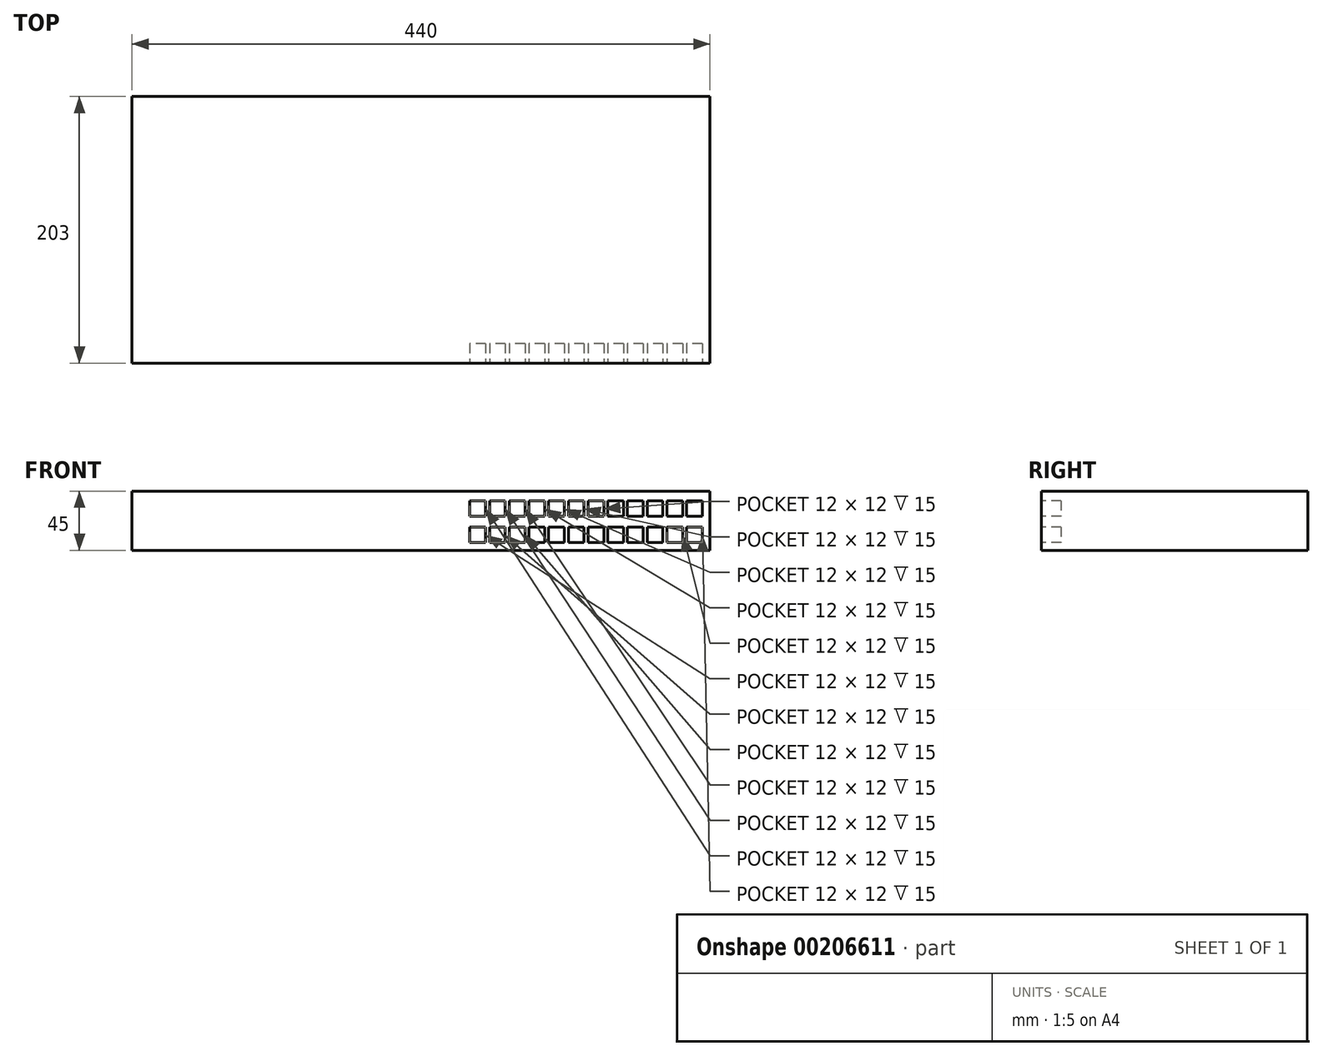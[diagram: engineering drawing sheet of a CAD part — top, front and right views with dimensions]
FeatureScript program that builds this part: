
annotation { "Feature Type Name" : "Feature", "Feature Type Description" : "" }
export const myFeature = defineFeature(function(context is Context, id is Id, definition is map)
    precondition{}
    {
        {
            var Q0;
            Q0=qCreatedBy(makeId("Front.planeOp"),FACE);
            var sketch = newSketch(context, id + "F0", { "sketchPlane" : qUnion([Q0])});
            skLineSegment(sketch, "E0.bottom", {"start": v(0, 0) * mm, "end": v(440, 0) * mm});
            skLineSegment(sketch, "E0.top", {"start": v(0, 45) * mm, "end": v(440, 45) * mm});
            skLineSegment(sketch, "E0.left", {"start": v(0, 0) * mm, "end": v(0, 45) * mm});
            skLineSegment(sketch, "E0.right", {"start": v(440, 0) * mm, "end": v(440, 45) * mm});
            skSolve(sketch);
        }
        {
            var Q0;
            Q0 = qSketchRegion(id + "F0", true);
            extrude(context, id + "F1", {"entities" : qUnion([Q0]), "depth" : 203 * mm});
        }
        {
            var Q0;
            Q0=makeQuery(id+"F1.opExtrude","CAP_FACE",FACE,{"disambiguationData":[OSD([sQuery(id+"F0.wireOp",EDGE,"E0.bottom"),sQuery(id+"F0.wireOp",EDGE,"E0.top"),sQuery(id+"F0.wireOp",EDGE,"E0.left"),sQuery(id+"F0.wireOp",EDGE,"E0.right")])],"isStart":false});
            var sketch = newSketch(context, id + "F2", { "sketchPlane" : qUnion([Q0])});
            skLineSegment(sketch, "E1", {"start": v(434.2, 37.78) * mm, "end": v(422.2, 37.78) * mm});
            skLineSegment(sketch, "E2", {"start": v(434.2, 37.78) * mm, "end": v(434.2, 25.78) * mm});
            skLineSegment(sketch, "E3.1.0.0", {"start": v(419.2, 37.78) * mm, "end": v(419.2, 25.78) * mm});
            skLineSegment(sketch, "E3.2.0.0", {"start": v(404.2, 37.78) * mm, "end": v(404.2, 25.78) * mm});
            skLineSegment(sketch, "E3.3.0.0", {"start": v(389.2, 37.78) * mm, "end": v(389.2, 25.78) * mm});
            skLineSegment(sketch, "E3.4.0.0", {"start": v(374.2, 37.78) * mm, "end": v(374.2, 25.78) * mm});
            skLineSegment(sketch, "E3.5.0.0", {"start": v(359.2, 37.78) * mm, "end": v(359.2, 25.78) * mm});
            skLineSegment(sketch, "E3.6.0.0", {"start": v(344.2, 37.78) * mm, "end": v(344.2, 25.78) * mm});
            skLineSegment(sketch, "E3.7.0.0", {"start": v(329.2, 37.78) * mm, "end": v(329.2, 25.78) * mm});
            skLineSegment(sketch, "E3.8.0.0", {"start": v(314.2, 37.78) * mm, "end": v(314.2, 25.78) * mm});
            skLineSegment(sketch, "E3.9.0.0", {"start": v(299.2, 37.78) * mm, "end": v(299.2, 25.78) * mm});
            skLineSegment(sketch, "E3.10.0.0", {"start": v(284.2, 37.78) * mm, "end": v(284.2, 25.78) * mm});
            skLineSegment(sketch, "E3.11.0.0", {"start": v(269.2, 37.78) * mm, "end": v(269.2, 25.78) * mm});
            skLineSegment(sketch, "E3.direction1", {"start": v(434.2, 5.78) * mm, "end": v(419.2, 5.78) * mm, "construction": true});
            skLineSegment(sketch, "E4.0", {"start": v(422.2, 37.78) * mm, "end": v(422.2, 25.78) * mm});
            skLineSegment(sketch, "E5.1.0.0", {"start": v(407.2, 37.78) * mm, "end": v(407.2, 25.78) * mm});
            skLineSegment(sketch, "E5.2.0.0", {"start": v(392.2, 37.78) * mm, "end": v(392.2, 25.78) * mm});
            skLineSegment(sketch, "E5.3.0.0", {"start": v(377.2, 37.78) * mm, "end": v(377.2, 25.78) * mm});
            skLineSegment(sketch, "E5.4.0.0", {"start": v(362.2, 37.78) * mm, "end": v(362.2, 25.78) * mm});
            skLineSegment(sketch, "E5.5.0.0", {"start": v(347.2, 37.78) * mm, "end": v(347.2, 25.78) * mm});
            skLineSegment(sketch, "E5.6.0.0", {"start": v(332.2, 37.78) * mm, "end": v(332.2, 25.78) * mm});
            skLineSegment(sketch, "E5.7.0.0", {"start": v(317.2, 37.78) * mm, "end": v(317.2, 25.78) * mm});
            skLineSegment(sketch, "E5.8.0.0", {"start": v(302.2, 37.78) * mm, "end": v(302.2, 25.78) * mm});
            skLineSegment(sketch, "E5.9.0.0", {"start": v(287.2, 37.78) * mm, "end": v(287.2, 25.78) * mm});
            skLineSegment(sketch, "E5.10.0.0", {"start": v(272.2, 37.78) * mm, "end": v(272.2, 25.78) * mm});
            skLineSegment(sketch, "E5.11.0.0", {"start": v(257.2, 37.78) * mm, "end": v(257.2, 25.78) * mm});
            skLineSegment(sketch, "E5.direction1", {"start": v(419.2, 5.78) * mm, "end": v(407.2, 5.78) * mm, "construction": true});
            skLineSegment(sketch, "E6", {"start": v(434.2, 25.78) * mm, "end": v(422.2, 25.78) * mm});
            skLineSegment(sketch, "E7", {"start": v(434.2, 17.78) * mm, "end": v(422.2, 17.78) * mm});
            skLineSegment(sketch, "E8", {"start": v(434.2, 5.78) * mm, "end": v(407.2, 5.78) * mm});
            skPoint(sketch, "E9.orphan", {"position": v(242.2, 38.76) * mm});
            skPoint(sketch, "E10.orphan", {"position": v(257.2, 38.76) * mm});
            skLineSegment(sketch, "E11.trimOffspring", {"start": v(269.2, 37.78) * mm, "end": v(257.2, 37.78) * mm});
            skPoint(sketch, "E12.orphan", {"position": v(272.2, 38.76) * mm});
            skLineSegment(sketch, "E13.trimOffspring", {"start": v(269.2, 25.78) * mm, "end": v(257.2, 25.78) * mm});
            skLineSegment(sketch, "E14.trimOffspring", {"start": v(269.2, 17.78) * mm, "end": v(269.2, 5.78) * mm});
            skLineSegment(sketch, "E15.trimOffspring", {"start": v(257.2, 17.78) * mm, "end": v(257.2, 5.78) * mm});
            skLineSegment(sketch, "E16.trimOffspring", {"start": v(272.2, 17.78) * mm, "end": v(272.2, 5.78) * mm});
            skLineSegment(sketch, "E17.trimOffspring", {"start": v(284.2, 17.78) * mm, "end": v(284.2, 5.78) * mm});
            skLineSegment(sketch, "E18.trimOffspring", {"start": v(287.2, 17.78) * mm, "end": v(287.2, 5.78) * mm});
            skLineSegment(sketch, "E19.trimOffspring", {"start": v(269.2, 17.78) * mm, "end": v(257.2, 17.78) * mm});
            skLineSegment(sketch, "E20.trimOffspring", {"start": v(269.2, 5.78) * mm, "end": v(257.2, 5.78) * mm});
            skLineSegment(sketch, "E21.trimOffspring", {"start": v(284.2, 17.78) * mm, "end": v(272.2, 17.78) * mm});
            skLineSegment(sketch, "E22.trimOffspring", {"start": v(299.2, 17.78) * mm, "end": v(299.2, 5.78) * mm});
            skLineSegment(sketch, "E23.trimOffspring", {"start": v(302.2, 17.78) * mm, "end": v(302.2, 5.78) * mm});
            skLineSegment(sketch, "E24.trimOffspring", {"start": v(314.2, 17.78) * mm, "end": v(314.2, 5.78) * mm});
            skLineSegment(sketch, "E25.trimOffspring", {"start": v(317.2, 17.78) * mm, "end": v(317.2, 5.78) * mm});
            skLineSegment(sketch, "E26.trimOffspring", {"start": v(314.2, 17.78) * mm, "end": v(302.2, 17.78) * mm});
            skLineSegment(sketch, "E27.trimOffspring", {"start": v(314.2, 5.78) * mm, "end": v(302.2, 5.78) * mm});
            skLineSegment(sketch, "E28.trimOffspring", {"start": v(299.2, 5.78) * mm, "end": v(272.2, 5.78) * mm});
            skLineSegment(sketch, "E29.trimOffspring", {"start": v(299.2, 17.78) * mm, "end": v(287.2, 17.78) * mm});
            skLineSegment(sketch, "E30.trimOffspring", {"start": v(299.2, 25.78) * mm, "end": v(287.2, 25.78) * mm});
            skLineSegment(sketch, "E31.trimOffspring", {"start": v(299.2, 37.78) * mm, "end": v(287.2, 37.78) * mm});
            skLineSegment(sketch, "E32.trimOffspring", {"start": v(314.2, 37.78) * mm, "end": v(302.2, 37.78) * mm});
            skLineSegment(sketch, "E33.trimOffspring", {"start": v(314.2, 25.78) * mm, "end": v(302.2, 25.78) * mm});
            skPoint(sketch, "E34.orphan", {"position": v(317.2, 38.76) * mm});
            skPoint(sketch, "E35.orphan", {"position": v(302.2, 38.76) * mm});
            skPoint(sketch, "E36.orphan", {"position": v(287.2, 38.76) * mm});
            skLineSegment(sketch, "E37.trimOffspring", {"start": v(284.2, 37.78) * mm, "end": v(272.2, 37.78) * mm});
            skLineSegment(sketch, "E38.trimOffspring", {"start": v(284.2, 25.78) * mm, "end": v(272.2, 25.78) * mm});
            skLineSegment(sketch, "E39.trimOffspring", {"start": v(329.2, 37.78) * mm, "end": v(317.2, 37.78) * mm});
            skLineSegment(sketch, "E40.trimOffspring", {"start": v(329.2, 25.78) * mm, "end": v(317.2, 25.78) * mm});
            skLineSegment(sketch, "E41.trimOffspring", {"start": v(329.2, 17.78) * mm, "end": v(317.2, 17.78) * mm});
            skLineSegment(sketch, "E42.trimOffspring", {"start": v(332.2, 17.78) * mm, "end": v(332.2, 5.78) * mm});
            skLineSegment(sketch, "E43.trimOffspring", {"start": v(329.2, 5.78) * mm, "end": v(317.2, 5.78) * mm});
            skLineSegment(sketch, "E44.trimOffspring", {"start": v(344.2, 5.78) * mm, "end": v(332.2, 5.78) * mm});
            skLineSegment(sketch, "E45.trimOffspring", {"start": v(344.2, 17.78) * mm, "end": v(332.2, 17.78) * mm});
            skLineSegment(sketch, "E46.trimOffspring", {"start": v(344.2, 25.78) * mm, "end": v(332.2, 25.78) * mm});
            skLineSegment(sketch, "E47.trimOffspring", {"start": v(329.2, 17.78) * mm, "end": v(329.2, 5.78) * mm});
            skLineSegment(sketch, "E48.trimOffspring", {"start": v(344.2, 17.78) * mm, "end": v(344.2, 5.78) * mm});
            skLineSegment(sketch, "E49.trimOffspring", {"start": v(347.2, 17.78) * mm, "end": v(347.2, 5.78) * mm});
            skLineSegment(sketch, "E50.trimOffspring", {"start": v(359.2, 17.78) * mm, "end": v(359.2, 5.78) * mm});
            skLineSegment(sketch, "E51.trimOffspring", {"start": v(362.2, 17.78) * mm, "end": v(362.2, 5.78) * mm});
            skLineSegment(sketch, "E52.trimOffspring", {"start": v(374.2, 17.78) * mm, "end": v(374.2, 5.78) * mm});
            skLineSegment(sketch, "E53.trimOffspring", {"start": v(377.2, 17.78) * mm, "end": v(377.2, 5.78) * mm});
            skLineSegment(sketch, "E54.trimOffspring", {"start": v(389.2, 17.78) * mm, "end": v(389.2, 5.78) * mm});
            skLineSegment(sketch, "E55.trimOffspring", {"start": v(407.2, 17.78) * mm, "end": v(407.2, 5.78) * mm});
            skLineSegment(sketch, "E56.trimOffspring", {"start": v(419.2, 17.78) * mm, "end": v(419.2, 5.78) * mm});
            skLineSegment(sketch, "E57.trimOffspring", {"start": v(422.2, 17.78) * mm, "end": v(422.2, 5.78) * mm});
            skLineSegment(sketch, "E58.trimOffspring", {"start": v(434.2, 17.78) * mm, "end": v(434.2, 5.78) * mm});
            skLineSegment(sketch, "E59.trimOffspring", {"start": v(419.2, 17.78) * mm, "end": v(407.2, 17.78) * mm});
            skLineSegment(sketch, "E60.trimOffspring", {"start": v(404.2, 17.78) * mm, "end": v(392.2, 17.78) * mm});
            skLineSegment(sketch, "E61.trimOffspring", {"start": v(404.2, 17.78) * mm, "end": v(404.2, 5.78) * mm});
            skLineSegment(sketch, "E62.trimOffspring", {"start": v(392.2, 17.78) * mm, "end": v(392.2, 5.78) * mm});
            skLineSegment(sketch, "E63.trimOffspring", {"start": v(389.2, 17.78) * mm, "end": v(377.2, 17.78) * mm});
            skLineSegment(sketch, "E64.trimOffspring", {"start": v(389.2, 5.78) * mm, "end": v(362.2, 5.78) * mm});
            skLineSegment(sketch, "E65.trimOffspring", {"start": v(404.2, 5.78) * mm, "end": v(392.2, 5.78) * mm});
            skLineSegment(sketch, "E66.trimOffspring", {"start": v(374.2, 17.78) * mm, "end": v(362.2, 17.78) * mm});
            skLineSegment(sketch, "E67.trimOffspring", {"start": v(359.2, 17.78) * mm, "end": v(347.2, 17.78) * mm});
            skLineSegment(sketch, "E68.trimOffspring", {"start": v(359.2, 5.78) * mm, "end": v(347.2, 5.78) * mm});
            skLineSegment(sketch, "E69.trimOffspring", {"start": v(419.2, 25.78) * mm, "end": v(407.2, 25.78) * mm});
            skLineSegment(sketch, "E70.trimOffspring", {"start": v(419.2, 37.78) * mm, "end": v(407.2, 37.78) * mm});
            skPoint(sketch, "E71.orphan", {"position": v(422.2, 38.76) * mm});
            skPoint(sketch, "E72.orphan", {"position": v(407.2, 38.76) * mm});
            skPoint(sketch, "E73.orphan", {"position": v(392.2, 38.76) * mm});
            skPoint(sketch, "E74.orphan", {"position": v(377.2, 38.76) * mm});
            skPoint(sketch, "E75.orphan", {"position": v(362.2, 38.76) * mm});
            skPoint(sketch, "E76.orphan", {"position": v(347.2, 38.76) * mm});
            skPoint(sketch, "E77.orphan", {"position": v(332.2, 38.76) * mm});
            skLineSegment(sketch, "E78.trimOffspring", {"start": v(344.2, 37.78) * mm, "end": v(332.2, 37.78) * mm});
            skLineSegment(sketch, "E79.trimOffspring", {"start": v(359.2, 25.78) * mm, "end": v(347.2, 25.78) * mm});
            skLineSegment(sketch, "E80.trimOffspring", {"start": v(359.2, 37.78) * mm, "end": v(347.2, 37.78) * mm});
            skLineSegment(sketch, "E81.trimOffspring", {"start": v(374.2, 37.78) * mm, "end": v(362.2, 37.78) * mm});
            skLineSegment(sketch, "E82.trimOffspring", {"start": v(374.2, 25.78) * mm, "end": v(362.2, 25.78) * mm});
            skLineSegment(sketch, "E83.trimOffspring", {"start": v(389.2, 37.78) * mm, "end": v(377.2, 37.78) * mm});
            skLineSegment(sketch, "E84.trimOffspring", {"start": v(404.2, 37.78) * mm, "end": v(392.2, 37.78) * mm});
            skLineSegment(sketch, "E85.trimOffspring", {"start": v(404.2, 25.78) * mm, "end": v(377.2, 25.78) * mm});
            skSolve(sketch);
        }
        {
            var Q0;
            Q0 = qSketchRegion(id + "F2", true);
            extrude(context, id + "F3", {"entities" : qUnion([Q0]), "operationType" : NewBodyOperationType.REMOVE, "oppositeDirection" : true, "depth" : 15 * mm});
        }
    });
